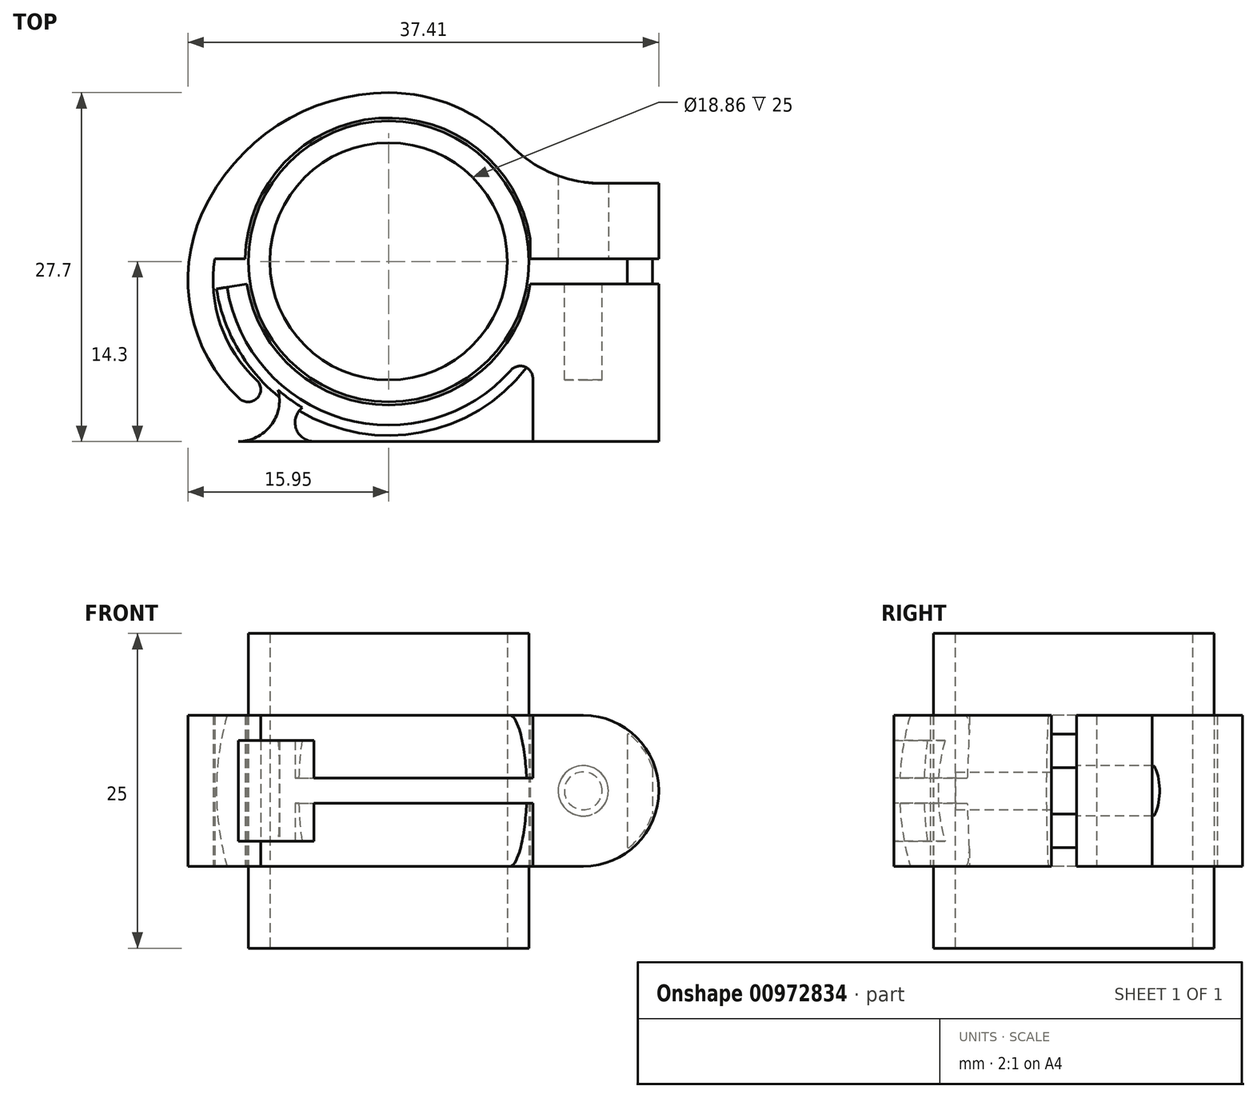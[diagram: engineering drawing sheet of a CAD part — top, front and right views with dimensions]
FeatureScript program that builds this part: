
annotation { "Feature Type Name" : "Feature", "Feature Type Description" : "" }
export const myFeature = defineFeature(function(context is Context, id is Id, definition is map)
    precondition{}
    {
        {
            var Q0;
            Q0=qCreatedBy(makeId("Top.planeOp"),FACE);
            var sketch = newSketch(context, id + "F0", { "sketchPlane" : qUnion([Q0])});
            skCircle(sketch, "E0", {"center": v(0, 0) * mm, "radius": 11.15 * mm});
            skCircle(sketch, "E1", {"center": v(0, 0) * mm, "radius": 9.43 * mm});
            skSolve(sketch);
        }
        {
            var Q0;
            Q0=makeQuery(id+"F0.imprint","IMPRINT",FACE,{"disambiguationData":[TD([[makeQuery(id+"F0.imprint","IMPRINT",EDGE,{"derivedFrom":sQuery(id+"F0.wireOp",EDGE,"E0")}),1.0]])]});
            extrude(context, id + "F1", {"entities" : qUnion([Q0]), "endBound" : BoundingType.SYMMETRIC, "depth" : 25 * mm, "offsetDistance" : 25 * mm});
        }
        {
            var Q0;
            Q0=qCreatedBy(makeId("Top.planeOp"),FACE);
            var sketch = newSketch(context, id + "F2", { "sketchPlane" : qUnion([Q0])});
            skArc(sketch, "E2", {"start": v(-11.26, -1.8) * mm, "mid": v(0, -11.4) * mm, "end": v(11.26, -1.8) * mm});
            skArc(sketch, "E3", {"start": v(-12.84, -2.05) * mm, "mid": v(-3.65, -12.48) * mm, "end": v(9.71, -8.64) * mm});
            skLineSegment(sketch, "E4", {"start": v(11.26, -1.8) * mm, "end": v(21.46, -1.8) * mm});
            skLineSegment(sketch, "E5", {"start": v(0, -13) * mm, "end": v(11.46, -13) * mm, "construction": true});
            skLineSegment(sketch, "E6", {"start": v(-13.68, -14.3) * mm, "end": v(21.46, -14.3) * mm});
            skLineSegment(sketch, "E7", {"start": v(-13.68, -2.19) * mm, "end": v(-11.26, -1.8) * mm});
            skLineSegment(sketch, "E8", {"start": v(11.26, -1.8) * mm, "end": v(-11.26, -1.8) * mm, "construction": true});
            skLineSegment(sketch, "E9", {"start": v(-13.29, -4.6) * mm, "end": v(-13.68, -2.19) * mm, "construction": true});
            skLineSegment(sketch, "E10", {"start": v(21.46, -1.8) * mm, "end": v(21.46, -14.3) * mm});
            skLineSegment(sketch, "E11", {"start": v(11.46, -9.3) * mm, "end": v(11.46, -14.3) * mm});
            skArc(sketch, "E12.filletArc", {"start": v(11.46, -9.3) * mm, "mid": v(10.81, -8.37) * mm, "end": v(9.71, -8.64) * mm});
            skArc(sketch, "E13", {"start": v(-11.94, -14.3) * mm, "mid": v(-8.95, -12.35) * mm, "end": v(-9.54, -8.83) * mm});
            skPoint(sketch, "E14", {"position": v(0, -11.4) * mm});
            skPoint(sketch, "E15", {"position": v(0, -13.85) * mm});
            skLineSegment(sketch, "E16", {"start": v(0, 0) * mm, "end": v(0, -13.85) * mm, "construction": true});
            skLineSegment(sketch, "E17", {"start": v(-8.68, -11.04) * mm, "end": v(-8.68, -14.3) * mm, "construction": true});
            skArc(sketch, "E18", {"start": v(-6.33, -11.35) * mm, "mid": v(-7.41, -13) * mm, "end": v(-5.93, -14.3) * mm});
            skArc(sketch, "E19", {"start": v(-13.68, -2.19) * mm, "mid": v(-3.41, -13.42) * mm, "end": v(10.97, -8.45) * mm});
            skSolve(sketch);
        }
        {
            var Q0;
            Q0=qCreatedBy(makeId("Right.planeOp"),FACE);
            var sketch = newSketch(context, id + "F3", { "sketchPlane" : qUnion([Q0])});
            skLineSegment(sketch, "E20.bottom", {"start": v(-11.4, 6) * mm, "end": v(-13, 6) * mm});
            skLineSegment(sketch, "E20.top", {"start": v(-11.4, -6) * mm, "end": v(-13, -6) * mm});
            skLineSegment(sketch, "E20.left", {"start": v(-11.4, 6) * mm, "end": v(-11.4, -6) * mm});
            skArc(sketch, "E21", {"start": v(-13, 6) * mm, "mid": v(-13.85, 0) * mm, "end": v(-13, -6) * mm});
            skPoint(sketch, "E22", {"position": v(-11.4, 0) * mm});
            skPoint(sketch, "E23", {"position": v(-13, 0) * mm});
            skPoint(sketch, "E24", {"position": v(-13.85, 0) * mm});
            skLineSegment(sketch, "E25", {"start": v(-11.4, 0) * mm, "end": v(-13.85, 0) * mm, "construction": true});
            skLineSegment(sketch, "E26", {"start": v(-13, 6) * mm, "end": v(-13, -6) * mm, "construction": true});
            skSolve(sketch);
        }
        {
            var Q0;
            {var subQ6=sQuery(id+"F2.wireOp",EDGE,"E2");Q0=makeQuery(id+"F2.imprint","IMPRINT",FACE,{"disambiguationData":[TD([[makeQuery(id+"F2.imprint","IMPRINT",EDGE,{"derivedFrom":subQ6}),-1.0]])]});}
            extrude(context, id + "F4", {"entities" : qUnion([Q0]), "endBound" : BoundingType.SYMMETRIC, "depth" : 12 * mm, "offsetDistance" : 25 * mm});
        }
        {
            var Q0;
            Q0=makeQuery(id+"F3.imprint","IMPRINT",FACE,{"disambiguationData":[TD([[makeQuery(id+"F3.imprint","IMPRINT",EDGE,{"derivedFrom":sQuery(id+"F3.wireOp",EDGE,"E20.bottom")}),1.0]])]});
            var Q1;
            Q1=sQuery(id+"F2.wireOp",EDGE,"E19");
            sweep(context, id + "F5", {"operationType" : NewBodyOperationType.ADD, "profiles" : qUnion([Q0]), "path" : qUnion([Q1])});
        }
        {
            var Q0;
            {var subQ5=sQuery(id+"F2.wireOp",EDGE,"E11");Q0=makeQuery(id+"F2.imprint","IMPRINT",FACE,{"disambiguationData":[TD([[makeQuery(id+"F2.imprint","IMPRINT",EDGE,{"derivedFrom":subQ5}),-1.0]])]});}
            var Q1;
            {var subQ0=sQuery(id+"F2.wireOp",EDGE,"E12.filletArc");var subQ1=sQuery(id+"F2.wireOp",EDGE,"E3");var subQ2=makeQuery(id+"F2.imprint","INTERSECT",VERTEX,{"derivedFrom":[subQ1,subQ0]});Q1=makeQuery(id+"F2.imprint","IMPRINT",FACE,{"disambiguationData":[TD([[makeQuery(id+"F2.imprint","IMPRINT",EDGE,{"disambiguationData":[TD([[subQ2,1.0]])],"derivedFrom":subQ1}),-1.0]])]});}
            var Q2;
            {var subQ0=sQuery(id+"F2.wireOp",EDGE,"E13");var subQ1=sQuery(id+"F2.wireOp",EDGE,"E3");var subQ2=makeQuery(id+"F2.imprint","INTERSECT",VERTEX,{"derivedFrom":[subQ1,subQ0]});Q2=makeQuery(id+"F2.imprint","IMPRINT",FACE,{"disambiguationData":[TD([[makeQuery(id+"F2.imprint","IMPRINT",EDGE,{"disambiguationData":[TD([[subQ2,-1.0]])],"derivedFrom":subQ1}),-1.0]])]});}
            var Q3;
            {var subQ0=sQuery(id+"F2.wireOp",EDGE,"E13");var subQ1=sQuery(id+"F2.wireOp",EDGE,"E6");var subQ2=makeQuery(id+"F2.imprint","INTERSECT",VERTEX,{"derivedFrom":[subQ1,subQ0]});Q3=makeQuery(id+"F2.imprint","IMPRINT",FACE,{"disambiguationData":[TD([[makeQuery(id+"F2.imprint","IMPRINT",EDGE,{"disambiguationData":[TD([[subQ2,-1.0]])],"derivedFrom":subQ1}),1.0]])]});}
            extrude(context, id + "F6", {"entities" : qUnion([Q0, Q1, Q2, Q3]), "operationType" : NewBodyOperationType.ADD, "endBound" : BoundingType.SYMMETRIC, "depth" : 2 * mm, "offsetDistance" : 25 * mm});
        }
        {
            var Q0;
            {var subQ0=sQuery(id+"F2.wireOp",EDGE,"E13");var subQ1=sQuery(id+"F2.wireOp",EDGE,"E3");var subQ2=makeQuery(id+"F2.imprint","INTERSECT",VERTEX,{"derivedFrom":[subQ1,subQ0]});Q0=makeQuery(id+"F2.imprint","IMPRINT",FACE,{"disambiguationData":[TD([[makeQuery(id+"F2.imprint","IMPRINT",EDGE,{"disambiguationData":[TD([[subQ2,-1.0]])],"derivedFrom":subQ1}),-1.0]])]});}
            var Q1;
            {var subQ0=sQuery(id+"F2.wireOp",EDGE,"E13");var subQ1=sQuery(id+"F2.wireOp",EDGE,"E6");var subQ2=makeQuery(id+"F2.imprint","INTERSECT",VERTEX,{"derivedFrom":[subQ1,subQ0]});Q1=makeQuery(id+"F2.imprint","IMPRINT",FACE,{"disambiguationData":[TD([[makeQuery(id+"F2.imprint","IMPRINT",EDGE,{"disambiguationData":[TD([[subQ2,-1.0]])],"derivedFrom":subQ1}),1.0]])]});}
            extrude(context, id + "F7", {"entities" : qUnion([Q0, Q1]), "operationType" : NewBodyOperationType.ADD, "endBound" : BoundingType.SYMMETRIC, "depth" : 8 * mm, "offsetDistance" : 25 * mm});
        }
        {
            var Q0;
            Q0=makeQuery(id+"F4.opExtrude","CAP_EDGE",EDGE,{"disambiguationData":[OSD([sQuery(id+"F2.wireOp",EDGE,"E10")])],"isStart":false});
            var Q1;
            Q1=makeQuery(id+"F4.opExtrude","CAP_EDGE",EDGE,{"disambiguationData":[OSD([sQuery(id+"F2.wireOp",EDGE,"E10")])],"isStart":true});
            fillet(context, id + "F8", {"entities" : qUnion([Q0, Q1]), "radius" : 6 * mm, "tangentPropagation" : true, "allowEdgeOverflow" : false});
        }
        {
            var Q0;
            Q0=makeQuery(id+"F4.opExtrude","SWEPT_FACE",FACE,{"disambiguationData":[OSD([sQuery(id+"F2.wireOp",EDGE,"E4")])]});
            extrude(context, id + "F9", {"entities" : qUnion([Q0]), "depth" : 8 * mm, "offsetDistance" : 25 * mm, "hasSecondDirection" : true, "secondDirectionOppositeDirection" : false, "secondDirectionDepth" : 2 * mm});
        }
        {
            var Q0;
            Q0=makeQuery(id+"F4.opExtrude","SWEPT_FACE",FACE,{"disambiguationData":[OSD([sQuery(id+"F2.wireOp",EDGE,"E4")])]});
            var sketch = newSketch(context, id + "F10", { "sketchPlane" : qUnion([Q0])});
            skCircle(sketch, "E27", {"center": v(-15.46, 0) * mm, "radius": 1.5 * mm});
            skArc(sketch, "E28", {"start": v(-18.96, 4.62) * mm, "mid": v(-20.17, 3.38) * mm, "end": v(-20.96, 1.84) * mm});
            skLineSegment(sketch, "E29", {"start": v(-18.96, 4.62) * mm, "end": v(-18.96, -4.62) * mm});
            skLineSegment(sketch, "E30", {"start": v(-20.96, 1.84) * mm, "end": v(-20.96, -1.84) * mm});
            skArc(sketch, "E31.trimOffspring", {"start": v(-20.96, -1.84) * mm, "mid": v(-20.17, -3.38) * mm, "end": v(-18.96, -4.62) * mm});
            skSolve(sketch);
        }
        {
            var Q0;
            Q0=makeQuery(id+"F10.imprint","IMPRINT",FACE,{"disambiguationData":[TD([[makeQuery(id+"F10.imprint","IMPRINT",EDGE,{"derivedFrom":sQuery(id+"F10.wireOp",EDGE,"E28")}),1.0]])]});
            extrude(context, id + "F11", {"entities" : qUnion([Q0]), "operationType" : NewBodyOperationType.ADD, "depth" : 2 * mm, "offsetDistance" : 25 * mm});
        }
        {
            var Q0;
            Q0=makeQuery(id+"F11.opExtrude","SWEPT_EDGE",EDGE,{"disambiguationData":[OSD([sQuery(id+"F10.wireOp",EDGE,"E28"),sQuery(id+"F10.wireOp",EDGE,"E29")])]});
            var Q1;
            Q1=makeQuery(id+"F11.opExtrude","SWEPT_EDGE",EDGE,{"disambiguationData":[OSD([sQuery(id+"F10.wireOp",EDGE,"E29"),sQuery(id+"F10.wireOp",EDGE,"E31.trimOffspring")])]});
            fillet(context, id + "F12", {"entities" : qUnion([Q0, Q1]), "radius" : 0.1 * mm, "tangentPropagation" : true, "allowEdgeOverflow" : false});
        }
        {
            var Q0;
            Q0=makeQuery(id+"F10.imprint","IMPRINT",FACE,{"disambiguationData":[TD([[makeQuery(id+"F10.imprint","IMPRINT",EDGE,{"derivedFrom":sQuery(id+"F10.wireOp",EDGE,"E27")}),1.0]])]});
            extrude(context, id + "F13", {"entities" : qUnion([Q0]), "operationType" : NewBodyOperationType.REMOVE, "oppositeDirection" : true, "depth" : 7.6 * mm, "offsetDistance" : 25 * mm});
        }
        {
            var Q0;
            Q0=qCreatedBy(makeId("Top.planeOp"),FACE);
            var sketch = newSketch(context, id + "F14", { "sketchPlane" : qUnion([Q0])});
            skLineSegment(sketch, "E32", {"start": v(0, 0) * mm, "end": v(0, 14.23) * mm, "construction": true});
            skLineSegment(sketch, "E33", {"start": v(0, 0) * mm, "end": v(15.58, 0) * mm, "construction": true});
            skLineSegment(sketch, "E34", {"start": v(0, 0) * mm, "end": v(-16.92, 3.9) * mm, "construction": true});
            skLineSegment(sketch, "E35", {"start": v(0, 0) * mm, "end": v(-14.3, -12.87) * mm, "construction": true});
            skArc(sketch, "E36", {"start": v(11.4, 0.2) * mm, "mid": v(7.99, 8.13) * mm, "end": v(0, 11.4) * mm});
            skArc(sketch, "E37", {"start": v(0, 11.4) * mm, "mid": v(-7.74, 9.12) * mm, "end": v(-13, 3) * mm});
            skArc(sketch, "E38", {"start": v(-13, 3) * mm, "mid": v(-13.73, -3.62) * mm, "end": v(-10.48, -9.43) * mm});
            skLineSegment(sketch, "E39", {"start": v(-11.26, -1.8) * mm, "end": v(-11.01, -1.76) * mm, "construction": true});
            skPoint(sketch, "E40", {"position": v(11.15, 0) * mm});
            skLineSegment(sketch, "E41", {"start": v(11.15, 0) * mm, "end": v(11.4, 0) * mm, "construction": true});
            skLineSegment(sketch, "E42", {"start": v(0, 11.4) * mm, "end": v(0, 11.15) * mm, "construction": true});
            skLineSegment(sketch, "E43", {"start": v(-13.68, -2.19) * mm, "end": v(-13.92, -2.23) * mm, "construction": true});
            skLineSegment(sketch, "E44", {"start": v(-10.48, -9.43) * mm, "end": v(-10.3, -9.27) * mm, "construction": true});
            skArc(sketch, "E45.1", {"start": v(13.4, 0.2) * mm, "mid": v(9.4, 9.55) * mm, "end": v(0, 13.4) * mm});
            skArc(sketch, "E45.2", {"start": v(0, 13.4) * mm, "mid": v(-8.82, 10.8) * mm, "end": v(-14.82, 3.82) * mm});
            skArc(sketch, "E45.3", {"start": v(-14.82, 3.82) * mm, "mid": v(-15.7, -4.02) * mm, "end": v(-11.84, -10.9) * mm});
            skArc(sketch, "E46", {"start": v(-11.84, -10.9) * mm, "mid": v(-10.43, -10.85) * mm, "end": v(-10.48, -9.43) * mm});
            skLineSegment(sketch, "E47", {"start": v(11.4, 0.2) * mm, "end": v(13.4, 0.2) * mm});
            skArc(sketch, "E48", {"start": v(0, 11.4) * mm, "mid": v(-7.99, 8.13) * mm, "end": v(-11.4, 0.2) * mm});
            skLineSegment(sketch, "E49", {"start": v(-11.4, 0.2) * mm, "end": v(-13.82, 0.2) * mm});
            skSolve(sketch);
        }
        {
            var Q0;
            Q0=makeQuery(id+"F14.imprint","IMPRINT",FACE,{"disambiguationData":[TD([[makeQuery(id+"F14.imprint","IMPRINT",EDGE,{"derivedFrom":sQuery(id+"F14.wireOp",EDGE,"E36")}),-1.0]])]});
            var Q1;
            {var subQ0=sQuery(id+"F14.wireOp",EDGE,"E37");Q1=makeQuery(id+"F14.imprint","IMPRINT",FACE,{"disambiguationData":[TD([[makeQuery(id+"F14.imprint","IMPRINT",EDGE,{"derivedFrom":subQ0}),1.0]])]});}
            extrude(context, id + "F15", {"entities" : qUnion([Q0, Q1]), "operationType" : NewBodyOperationType.ADD, "endBound" : BoundingType.SYMMETRIC, "depth" : 12 * mm, "offsetDistance" : 25 * mm});
        }
        {
            var Q0;
            Q0=makeQuery(id+"F15.boolean.opBoolean","INTERSECT",EDGE,{"derivedFrom":[makeQuery(id+"F9.opExtrude","CAP_FACE",FACE,{"disambiguationData":[OSD([sQuery(id+"F2.wireOp",EDGE,"E4")])],"isStart":false}),makeQuery(id+"F15.opExtrude","SWEPT_FACE",FACE,{"disambiguationData":[OSD([sQuery(id+"F14.wireOp",EDGE,"E45.1")])]})]});
            fillet(context, id + "F16", {"entities" : qUnion([Q0]), "radius" : 10 * mm, "tangentPropagation" : true, "allowEdgeOverflow" : false});
        }
        {
            var Q0;
            Q0=makeQuery(id+"F9.opExtrude","CAP_FACE",FACE,{"disambiguationData":[OSD([sQuery(id+"F2.wireOp",EDGE,"E4")])],"isStart":true});
            var sketch = newSketch(context, id + "F17", { "sketchPlane" : qUnion([Q0])});
            skCircle(sketch, "E50.0", {"center": v(15.46, 0) * mm, "radius": 1.5 * mm, "construction": true});
            skCircle(sketch, "E51", {"center": v(15.46, 0) * mm, "radius": 2 * mm});
            skSolve(sketch);
        }
        {
            var Q0;
            Q0=makeQuery(id+"F17.imprint","IMPRINT",FACE,{"disambiguationData":[TD([[makeQuery(id+"F17.imprint","IMPRINT",EDGE,{"derivedFrom":sQuery(id+"F17.wireOp",EDGE,"E51")}),1.0]])]});
            extrude(context, id + "F18", {"entities" : qUnion([Q0]), "operationType" : NewBodyOperationType.REMOVE, "oppositeDirection" : true, "depth" : 25 * mm, "offsetDistance" : 25 * mm});
        }
    });
